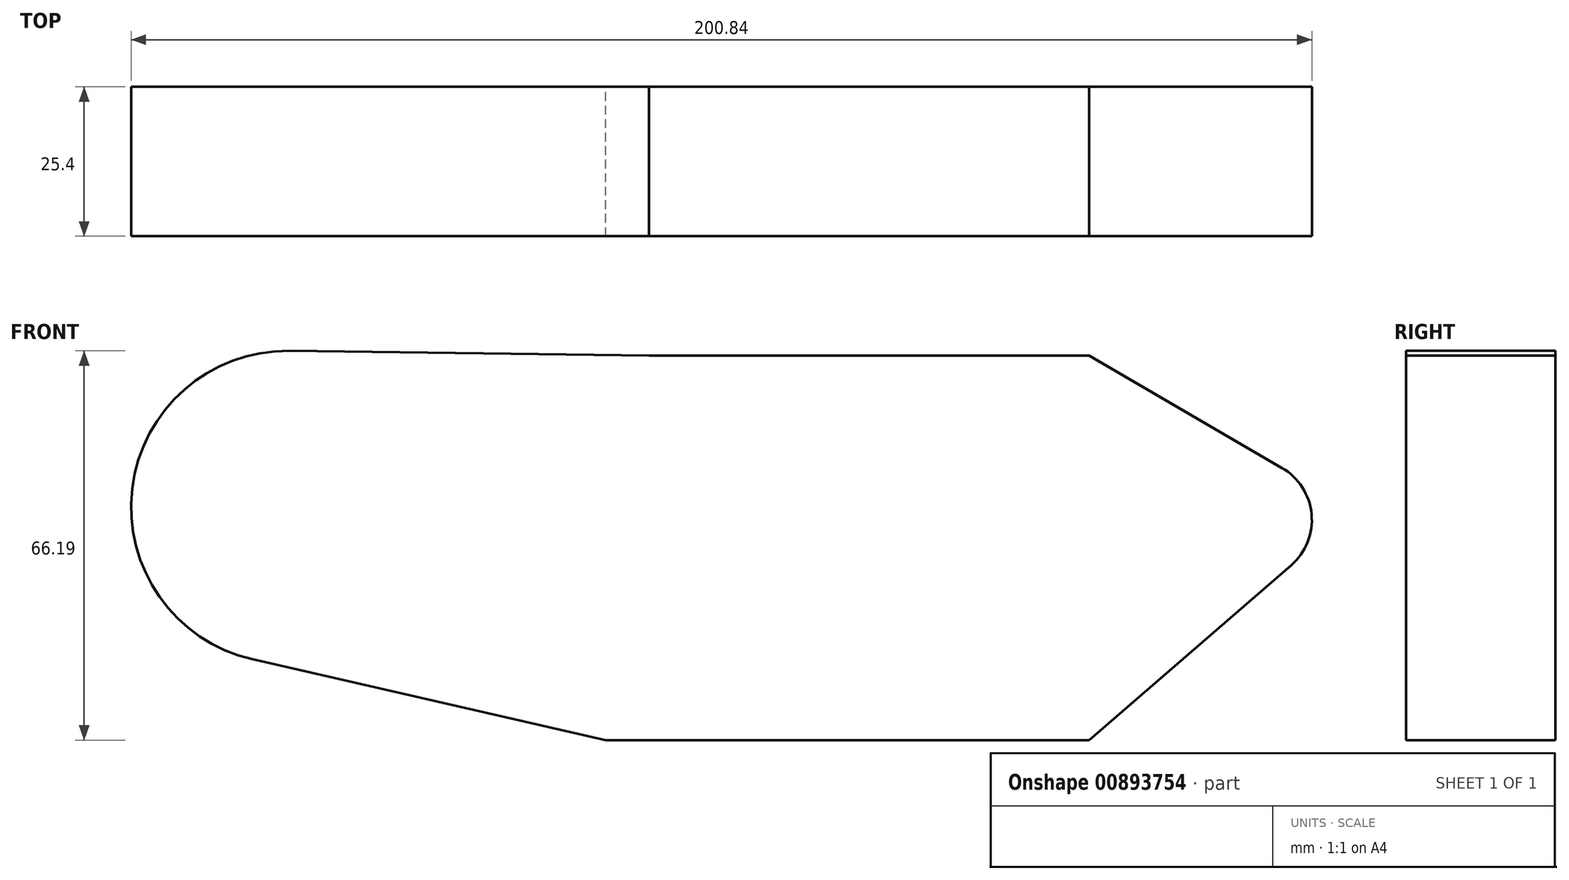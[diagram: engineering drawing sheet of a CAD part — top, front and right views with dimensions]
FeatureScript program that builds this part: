
annotation { "Feature Type Name" : "Feature", "Feature Type Description" : "" }
export const myFeature = defineFeature(function(context is Context, id is Id, definition is map)
    precondition{}
    {
        {
            var Q0;
            Q0=qCreatedBy(makeId("Front.planeOp"),FACE);
            var sketch = newSketch(context, id + "F0", { "sketchPlane" : qUnion([Q0])});
            skCircle(sketch, "E0", {"center": v(-107.74, 7.45) * mm, "radius": 26.57 * mm});
            skCircle(sketch, "E1", {"center": v(56.29, 5.28) * mm, "radius": 10.24 * mm});
            skLineSegment(sketch, "E2.bottom", {"start": v(-53.62, 33.2) * mm, "end": v(28.63, 33.2) * mm});
            skLineSegment(sketch, "E2.top", {"start": v(-53.62, -32.17) * mm, "end": v(28.63, -32.17) * mm});
            skLineSegment(sketch, "E2.left", {"start": v(-53.62, 33.2) * mm, "end": v(-53.62, -32.17) * mm});
            skLineSegment(sketch, "E2.right", {"start": v(28.63, 33.2) * mm, "end": v(28.63, -32.17) * mm});
            skLineSegment(sketch, "E3", {"start": v(-107.4, 34.02) * mm, "end": v(-46.2, 33.2) * mm});
            skLineSegment(sketch, "E4", {"start": v(-46.2, 33.2) * mm, "end": v(28.63, 33.2) * mm});
            skLineSegment(sketch, "E5", {"start": v(61.43, 14.13) * mm, "end": v(28.63, 33.2) * mm});
            skLineSegment(sketch, "E6", {"start": v(62.98, -2.47) * mm, "end": v(28.63, -32.17) * mm});
            skLineSegment(sketch, "E7", {"start": v(-53.62, -32.17) * mm, "end": v(-113.67, -18.45) * mm});
            skSolve(sketch);
        }
        {
            var Q0;
            Q0 = qSketchRegion(id + "F0", true);
            extrude(context, id + "F1", {"entities" : qUnion([Q0]), "depth" : 25.4 * mm, "offsetDistance" : 25.4 * mm});
        }
    });
